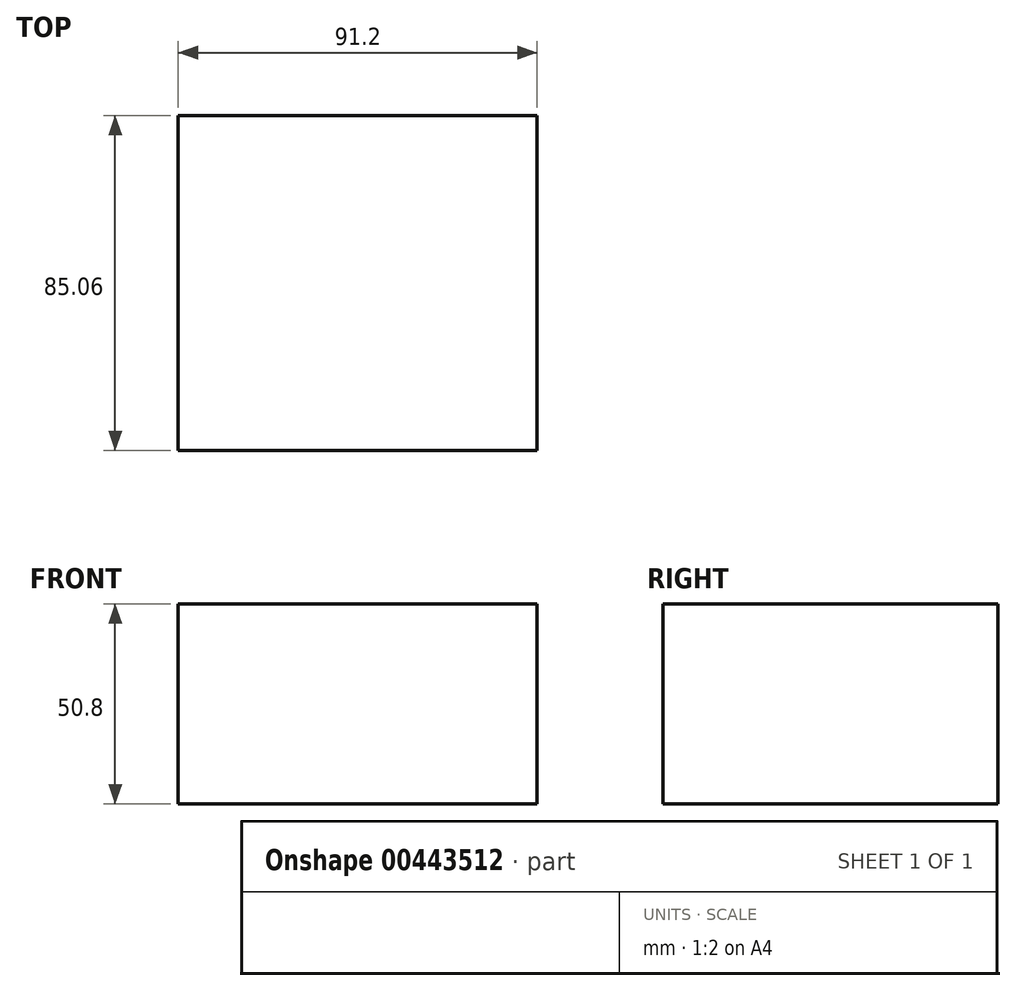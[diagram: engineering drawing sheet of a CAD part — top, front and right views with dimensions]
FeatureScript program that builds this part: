
annotation { "Feature Type Name" : "Feature", "Feature Type Description" : "" }
export const myFeature = defineFeature(function(context is Context, id is Id, definition is map)
    precondition{}
    {
        {
            var Q0;
            Q0=qCreatedBy(makeId("Top.planeOp"),FACE);
            var sketch = newSketch(context, id + "F0", { "sketchPlane" : qUnion([Q0])});
            skLineSegment(sketch, "E0.bottom", {"start": v(45.6, 42.53) * mm, "end": v(-45.6, 42.53) * mm});
            skLineSegment(sketch, "E0.top", {"start": v(45.6, -42.53) * mm, "end": v(-45.6, -42.53) * mm});
            skLineSegment(sketch, "E0.left", {"start": v(45.6, 42.53) * mm, "end": v(45.6, -42.53) * mm});
            skLineSegment(sketch, "E0.right", {"start": v(-45.6, 42.53) * mm, "end": v(-45.6, -42.53) * mm});
            skPoint(sketch, "E0.middle", {"position": v(0, 0) * mm});
            skSolve(sketch);
        }
        {
            var Q0;
            Q0 = qSketchRegion(id + "F0", true);
            extrude(context, id + "F1", {"entities" : qUnion([Q0]), "depth" : 50.8 * mm});
        }
    });
